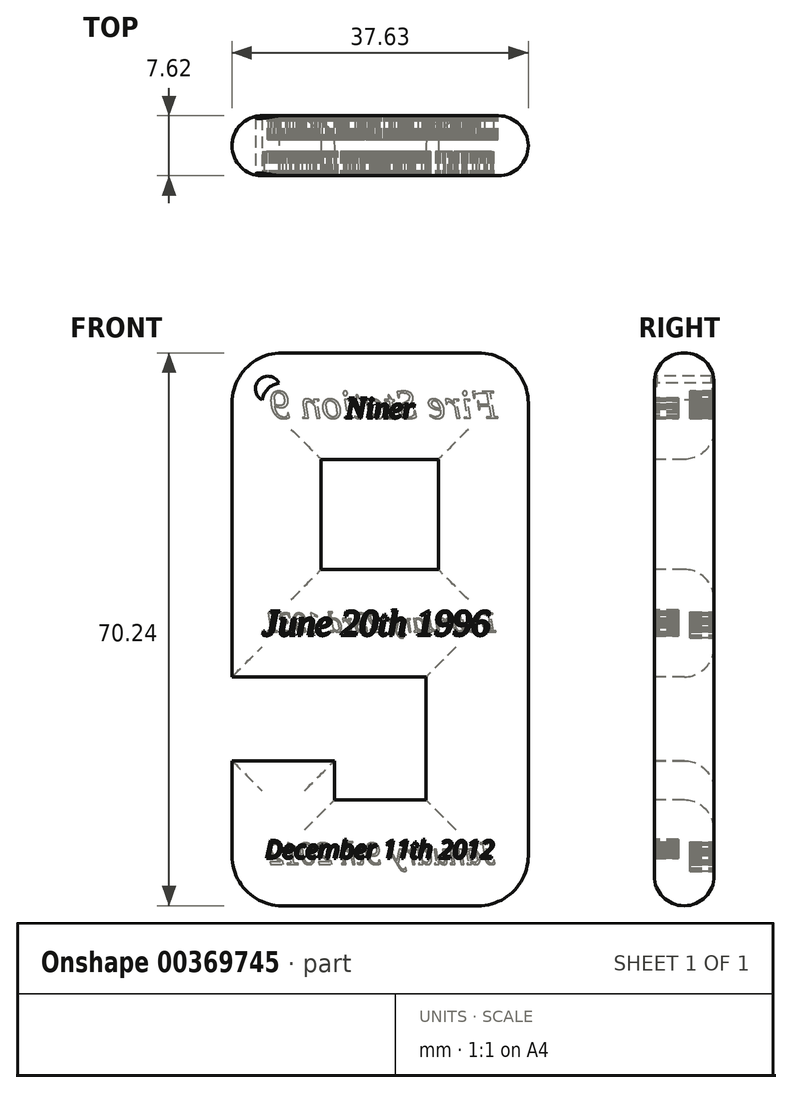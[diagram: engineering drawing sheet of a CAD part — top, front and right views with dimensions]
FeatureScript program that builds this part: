
annotation { "Feature Type Name" : "Feature", "Feature Type Description" : "" }
export const myFeature = defineFeature(function(context is Context, id is Id, definition is map)
    precondition{}
    {
        {
            var Q0;
            Q0=qCreatedBy(makeId("Front.planeOp"),FACE);
            var sketch = newSketch(context, id + "F0", { "sketchPlane" : qUnion([Q0])});
            skLineSegment(sketch, "E0.bottom", {"start": v(-12.42, 34.84) * mm, "end": v(12.5, 34.84) * mm});
            skLineSegment(sketch, "E0.top", {"start": v(-12.42, -35.4) * mm, "end": v(12.5, -35.4) * mm});
            skLineSegment(sketch, "E0.left", {"start": v(-18.77, 28.49) * mm, "end": v(-18.77, -29.05) * mm});
            skLineSegment(sketch, "E0.right", {"start": v(18.86, 28.49) * mm, "end": v(18.86, -29.05) * mm});
            skPoint(sketch, "E1.visualSharp", {"position": v(18.86, 34.84) * mm});
            skArc(sketch, "E1.filletArc", {"start": v(18.86, 28.49) * mm, "mid": v(17, 32.98) * mm, "end": v(12.5, 34.84) * mm});
            skPoint(sketch, "E2.visualSharp", {"position": v(18.86, -35.4) * mm});
            skArc(sketch, "E2.filletArc", {"start": v(12.5, -35.4) * mm, "mid": v(17, -33.54) * mm, "end": v(18.86, -29.05) * mm});
            skPoint(sketch, "E3.visualSharp", {"position": v(-18.77, -35.4) * mm});
            skArc(sketch, "E3.filletArc", {"start": v(-18.77, -29.05) * mm, "mid": v(-16.9, -33.54) * mm, "end": v(-12.42, -35.4) * mm});
            skPoint(sketch, "E4.visualSharp", {"position": v(-18.77, 34.84) * mm});
            skArc(sketch, "E4.filletArc", {"start": v(-12.42, 34.84) * mm, "mid": v(-16.9, 32.98) * mm, "end": v(-18.77, 28.49) * mm});
            skSolve(sketch);
        }
        {
            var Q0;
            Q0 = qSketchRegion(id + "F0", true);
            extrude(context, id + "F1", {"entities" : qUnion([Q0]), "depth" : 7.62 * mm});
        }
        {
            var Q0;
            Q0=makeQuery(id+"F1.opExtrude","CAP_FACE",FACE,{"disambiguationData":[OSD([sQuery(id+"F0.wireOp",EDGE,"E0.bottom"),sQuery(id+"F0.wireOp",EDGE,"E0.top"),sQuery(id+"F0.wireOp",EDGE,"E0.left"),sQuery(id+"F0.wireOp",EDGE,"E0.right")])],"isStart":false});
            var sketch = newSketch(context, id + "F2", { "sketchPlane" : qUnion([Q0])});
            skLineSegment(sketch, "E5.bottom", {"start": v(-7.43, 7.32) * mm, "end": v(7.43, 7.32) * mm});
            skLineSegment(sketch, "E5.top", {"start": v(-7.43, 21.3) * mm, "end": v(7.43, 21.3) * mm});
            skLineSegment(sketch, "E5.left", {"start": v(-7.43, 7.32) * mm, "end": v(-7.43, 21.3) * mm});
            skLineSegment(sketch, "E5.right", {"start": v(7.43, 7.32) * mm, "end": v(7.43, 21.3) * mm});
            skPoint(sketch, "E5.middle", {"position": v(0, 14.32) * mm});
            skSolve(sketch);
        }
        {
            var Q0;
            Q0 = qSketchRegion(id + "F2", true);
            extrude(context, id + "F3", {"entities" : qUnion([Q0]), "operationType" : NewBodyOperationType.REMOVE, "oppositeDirection" : true, "depth" : 7.62 * mm});
        }
        {
            var Q0;
            Q0=makeQuery(id+"F1.opExtrude","CAP_FACE",FACE,{"disambiguationData":[OSD([sQuery(id+"F0.wireOp",EDGE,"E0.bottom"),sQuery(id+"F0.wireOp",EDGE,"E0.top"),sQuery(id+"F0.wireOp",EDGE,"E0.left"),sQuery(id+"F0.wireOp",EDGE,"E0.right")])],"isStart":false});
            var sketch = newSketch(context, id + "F4", { "sketchPlane" : qUnion([Q0])});
            skLineSegment(sketch, "E6.bottom", {"start": v(-53.69, -16.98) * mm, "end": v(-3.13, -16.98) * mm});
            skLineSegment(sketch, "E6.top", {"start": v(-53.69, -6.33) * mm, "end": v(-3.13, -6.33) * mm});
            skLineSegment(sketch, "E6.left", {"start": v(-53.69, -16.98) * mm, "end": v(-53.69, -6.33) * mm});
            skLineSegment(sketch, "E6.right", {"start": v(-3.13, -16.98) * mm, "end": v(-3.13, -6.33) * mm});
            skPoint(sketch, "E6.middle", {"position": v(-28.4, -11.65) * mm});
            skLineSegment(sketch, "E7.bottom", {"start": v(5.88, -6.33) * mm, "end": v(-5.77, -6.33) * mm});
            skLineSegment(sketch, "E7.top", {"start": v(5.88, -21.97) * mm, "end": v(-5.77, -21.97) * mm});
            skLineSegment(sketch, "E7.left", {"start": v(5.88, -6.33) * mm, "end": v(5.88, -21.97) * mm});
            skLineSegment(sketch, "E7.right", {"start": v(-5.77, -6.33) * mm, "end": v(-5.77, -21.97) * mm});
            skSolve(sketch);
        }
        {
            var Q0;
            Q0 = qSketchRegion(id + "F4", true);
            extrude(context, id + "F5", {"entities" : qUnion([Q0]), "operationType" : NewBodyOperationType.REMOVE, "oppositeDirection" : true, "depth" : 7.62 * mm});
        }
        {
            var Q0;
            Q0=makeQuery(id+"F1.opExtrude","CAP_FACE",FACE,{"disambiguationData":[OSD([sQuery(id+"F0.wireOp",EDGE,"E0.bottom"),sQuery(id+"F0.wireOp",EDGE,"E0.top"),sQuery(id+"F0.wireOp",EDGE,"E0.left"),sQuery(id+"F0.wireOp",EDGE,"E0.right"),sQuery(id+"F0.wireOp",EDGE,"E1.filletArc"),sQuery(id+"F0.wireOp",EDGE,"E2.filletArc"),sQuery(id+"F0.wireOp",EDGE,"E3.filletArc"),sQuery(id+"F0.wireOp",EDGE,"E4.filletArc")])],"isStart":false});
            var sketch = newSketch(context, id + "F6", { "sketchPlane" : qUnion([Q0])});
            skPoint(sketch, "E8", {"position": v(0, 34.84) * mm});
            skPoint(sketch, "E9", {"position": v(0, 21.3) * mm});
            skPoint(sketch, "E10", {"position": v(-7.43, 14.32) * mm});
            skPoint(sketch, "E11", {"position": v(-18.77, 14.32) * mm});
            skPoint(sketch, "E12", {"position": v(7.43, 14.32) * mm});
            skPoint(sketch, "E13", {"position": v(18.86, 14.32) * mm});
            skPoint(sketch, "E14", {"position": v(0, -6.33) * mm});
            skPoint(sketch, "E15", {"position": v(0, 7.32) * mm});
            skSolve(sketch);
        }
        {
            var Q0;
            {var subQ0=sQuery(id+"F0.wireOp",EDGE,"E4.filletArc");var subQ1=sQuery(id+"F0.wireOp",EDGE,"E0.left");Q0=makeQuery(id+"F5.boolean.opBoolean","SPLIT",EDGE,{"disambiguationData":[TD([makeQuery(id+"F1.opExtrude","SWEPT_FACE",FACE,{"disambiguationData":[OSD([subQ0])]})])],"derivedFrom":makeQuery(id+"F1.opExtrude","CAP_EDGE",EDGE,{"disambiguationData":[OSD([subQ1])],"isStart":false})});}
            var Q1;
            Q1=makeQuery(id+"F5.boolean.opBoolean","COPY",EDGE,{"derivedFrom":makeQuery(id+"F5.opExtrude","CAP_EDGE",EDGE,{"disambiguationData":[OSD([sQuery(id+"F4.wireOp",EDGE,"E6.top"),sQuery(id+"F4.wireOp",EDGE,"E7.bottom")])],"isStart":true})});
            var Q2;
            {var subQ0=sQuery(id+"F0.wireOp",EDGE,"E3.filletArc");var subQ1=sQuery(id+"F0.wireOp",EDGE,"E0.left");Q2=makeQuery(id+"F5.boolean.opBoolean","SPLIT",EDGE,{"disambiguationData":[TD([makeQuery(id+"F1.opExtrude","SWEPT_FACE",FACE,{"disambiguationData":[OSD([subQ0])]})])],"derivedFrom":makeQuery(id+"F1.opExtrude","CAP_EDGE",EDGE,{"disambiguationData":[OSD([subQ1])],"isStart":false})});}
            var Q3;
            Q3=makeQuery(id+"F5.boolean.opBoolean","COPY",EDGE,{"derivedFrom":makeQuery(id+"F5.opExtrude","CAP_EDGE",EDGE,{"disambiguationData":[OSD([sQuery(id+"F4.wireOp",EDGE,"E6.bottom")])],"isStart":true})});
            var Q4;
            Q4=makeQuery(id+"F5.boolean.opBoolean","COPY",EDGE,{"derivedFrom":makeQuery(id+"F5.opExtrude","CAP_EDGE",EDGE,{"disambiguationData":[OSD([sQuery(id+"F4.wireOp",EDGE,"E7.right")])],"isStart":true})});
            var Q5;
            Q5=makeQuery(id+"F5.boolean.opBoolean","COPY",EDGE,{"derivedFrom":makeQuery(id+"F5.opExtrude","CAP_EDGE",EDGE,{"disambiguationData":[OSD([sQuery(id+"F4.wireOp",EDGE,"E7.top")])],"isStart":true})});
            var Q6;
            Q6=makeQuery(id+"F5.boolean.opBoolean","COPY",EDGE,{"derivedFrom":makeQuery(id+"F5.opExtrude","CAP_EDGE",EDGE,{"disambiguationData":[OSD([sQuery(id+"F4.wireOp",EDGE,"E7.left")])],"isStart":true})});
            var Q7;
            Q7=makeQuery(id+"F3.boolean.opBoolean","COPY",EDGE,{"derivedFrom":makeQuery(id+"F3.opExtrude","CAP_EDGE",EDGE,{"disambiguationData":[OSD([sQuery(id+"F2.wireOp",EDGE,"E5.left")])],"isStart":true})});
            var Q8;
            Q8=makeQuery(id+"F3.boolean.opBoolean","COPY",EDGE,{"derivedFrom":makeQuery(id+"F3.opExtrude","CAP_EDGE",EDGE,{"disambiguationData":[OSD([sQuery(id+"F2.wireOp",EDGE,"E5.top")])],"isStart":true})});
            var Q9;
            Q9=makeQuery(id+"F3.boolean.opBoolean","COPY",EDGE,{"derivedFrom":makeQuery(id+"F3.opExtrude","CAP_EDGE",EDGE,{"disambiguationData":[OSD([sQuery(id+"F2.wireOp",EDGE,"E5.right")])],"isStart":true})});
            var Q10;
            Q10=makeQuery(id+"F3.boolean.opBoolean","COPY",EDGE,{"derivedFrom":makeQuery(id+"F3.opExtrude","CAP_EDGE",EDGE,{"disambiguationData":[OSD([sQuery(id+"F2.wireOp",EDGE,"E5.bottom")])],"isStart":true})});
            fillet(context, id + "F7", {"entities" : qUnion([Q0, Q1, Q2, Q3, Q4, Q5, Q6, Q7, Q8, Q9, Q10]), "radius" : 3.8 * mm, "tangentPropagation" : true, "allowEdgeOverflow" : false});
        }
        {
            var Q0;
            Q0=makeQuery(id+"F1.opExtrude","CAP_FACE",FACE,{"disambiguationData":[OSD([sQuery(id+"F0.wireOp",EDGE,"E0.bottom"),sQuery(id+"F0.wireOp",EDGE,"E0.top"),sQuery(id+"F0.wireOp",EDGE,"E0.left"),sQuery(id+"F0.wireOp",EDGE,"E0.right"),sQuery(id+"F0.wireOp",EDGE,"E1.filletArc"),sQuery(id+"F0.wireOp",EDGE,"E2.filletArc"),sQuery(id+"F0.wireOp",EDGE,"E3.filletArc"),sQuery(id+"F0.wireOp",EDGE,"E4.filletArc")])],"isStart":true});
            fillet(context, id + "F8", {"entities" : qUnion([Q0]), "radius" : 3.8 * mm, "tangentPropagation" : true, "allowEdgeOverflow" : false});
        }
        {
            var Q0;
            Q0=makeQuery(id+"F1.opExtrude","CAP_FACE",FACE,{"disambiguationData":[OSD([sQuery(id+"F0.wireOp",EDGE,"E0.bottom"),sQuery(id+"F0.wireOp",EDGE,"E0.top"),sQuery(id+"F0.wireOp",EDGE,"E0.left"),sQuery(id+"F0.wireOp",EDGE,"E0.right"),sQuery(id+"F0.wireOp",EDGE,"E1.filletArc"),sQuery(id+"F0.wireOp",EDGE,"E2.filletArc"),sQuery(id+"F0.wireOp",EDGE,"E3.filletArc"),sQuery(id+"F0.wireOp",EDGE,"E4.filletArc")])],"isStart":true});
            var sketch = newSketch(context, id + "F9", { "sketchPlane" : qUnion([Q0])});
            skText(sketch, "E16", { "text": "Fire Station 9", "fontName": "Tinos-Italic.ttf"});
            const initialGuessF9  = {"E16": [-0.015, 0.02653, 1, 0, 0.00375]};
            skSetInitialGuess(sketch, initialGuessF9);
            skSolve(sketch);
        }
        {
            var Q0;
            Q0 = qSketchRegion(id + "F9", true);
            extrude(context, id + "F10", {"entities" : qUnion([Q0]), "operationType" : NewBodyOperationType.REMOVE, "oppositeDirection" : true, "depth" : 3.05 * mm});
        }
        {
            var Q0;
            {var subQ0=sQuery(id+"F0.wireOp",EDGE,"E4.filletArc");var subQ1=sQuery(id+"F0.wireOp",EDGE,"E3.filletArc");var subQ2=sQuery(id+"F0.wireOp",EDGE,"E2.filletArc");var subQ3=sQuery(id+"F0.wireOp",EDGE,"E1.filletArc");var subQ4=sQuery(id+"F0.wireOp",EDGE,"E0.right");var subQ5=sQuery(id+"F0.wireOp",EDGE,"E0.left");var subQ6=sQuery(id+"F0.wireOp",EDGE,"E0.top");var subQ7=sQuery(id+"F0.wireOp",EDGE,"E0.bottom");var subQ8=makeQuery(id+"F1.opExtrude","CAP_FACE",FACE,{"disambiguationData":[OSD([subQ7,subQ6,subQ5,subQ4,subQ3,subQ2,subQ1,subQ0])],"isStart":false});Q0=makeQuery(id+"FmLQ3wYA3wTMYqe_1.boolean.opBoolean","SPLIT",FACE,{"disambiguationData":[TD([makeQuery(id+"F7.opFillet","BLEND_FACE",FACE,{"disambiguationData":[OSD([subQ7])]})])],"derivedFrom":subQ8});}
            var sketch = newSketch(context, id + "F11", { "sketchPlane" : qUnion([Q0])});
            skCircle(sketch, "E17", {"center": v(-14.21, 30.28) * mm, "radius": 1.6 * mm});
            skSolve(sketch);
        }
        {
            var Q0;
            {var subQ0=sQuery(id+"F11.wireOp",EDGE,"E17");var subQ1=sQuery(id+"F0.wireOp",EDGE,"E4.filletArc");var subQ2=makeQuery(id+"F7.opFillet","BLEND_EDGE",EDGE,{"blendedFrom":[makeQuery(id+"F1.opExtrude","CAP_EDGE",EDGE,{"disambiguationData":[OSD([subQ1])],"isStart":false}),makeQuery(id+"F1.opExtrude","CAP_FACE",FACE,{"disambiguationData":[OSD([sQuery(id+"F0.wireOp",EDGE,"E0.bottom"),sQuery(id+"F0.wireOp",EDGE,"E0.top"),sQuery(id+"F0.wireOp",EDGE,"E0.left"),sQuery(id+"F0.wireOp",EDGE,"E0.right"),sQuery(id+"F0.wireOp",EDGE,"E1.filletArc"),sQuery(id+"F0.wireOp",EDGE,"E2.filletArc"),sQuery(id+"F0.wireOp",EDGE,"E3.filletArc"),subQ1])],"isStart":false})],"blendedInto":[makeQuery(id+"F1.opExtrude","CAP_FACE",FACE,{"disambiguationData":[OSD([sQuery(id+"F0.wireOp",EDGE,"E0.bottom"),sQuery(id+"F0.wireOp",EDGE,"E0.top"),sQuery(id+"F0.wireOp",EDGE,"E0.left"),sQuery(id+"F0.wireOp",EDGE,"E0.right"),sQuery(id+"F0.wireOp",EDGE,"E1.filletArc"),sQuery(id+"F0.wireOp",EDGE,"E2.filletArc"),sQuery(id+"F0.wireOp",EDGE,"E3.filletArc"),subQ1])],"isStart":false})]});var subQ3=makeQuery(id+"F11.imprint","INTERSECT",VERTEX,{"disambiguationData":[OD(0.0)],"derivedFrom":[subQ2,subQ0]});Q0=makeQuery(id+"F11.imprint","IMPRINT",FACE,{"disambiguationData":[TD([[makeQuery(id+"F11.imprint","IMPRINT",EDGE,{"disambiguationData":[TD([[subQ3,-1.0]])],"derivedFrom":subQ0}),1.0]])]});}
            extrude(context, id + "F12", {"entities" : qUnion([Q0]), "operationType" : NewBodyOperationType.REMOVE, "oppositeDirection" : true, "depth" : 25.4 * mm});
        }
        {
            var Q0;
            Q0=makeQuery(id+"F1.opExtrude","CAP_FACE",FACE,{"disambiguationData":[OSD([sQuery(id+"F0.wireOp",EDGE,"E0.bottom"),sQuery(id+"F0.wireOp",EDGE,"E0.top"),sQuery(id+"F0.wireOp",EDGE,"E0.left"),sQuery(id+"F0.wireOp",EDGE,"E0.right"),sQuery(id+"F0.wireOp",EDGE,"E1.filletArc"),sQuery(id+"F0.wireOp",EDGE,"E2.filletArc"),sQuery(id+"F0.wireOp",EDGE,"E3.filletArc"),sQuery(id+"F0.wireOp",EDGE,"E4.filletArc")])],"isStart":false});
            var sketch = newSketch(context, id + "F13", { "sketchPlane" : qUnion([Q0])});
            skText(sketch, "E18", { "text": "Niner", "fontName": "Tinos-Italic.ttf"});
            const initialGuessF13  = {"E18": [-0.00433, 0.02656, 1, 0, 0.00276]};
            skSetInitialGuess(sketch, initialGuessF13);
            skSolve(sketch);
        }
        {
            var Q0;
            Q0=makeQuery(id+"F13.imprint","IMPRINT",FACE,{"disambiguationData":[TD([[makeQuery(id+"F13.imprint","IMPRINT",EDGE,{"derivedFrom":sQuery(id+"F13.wireOp",EDGE,"E18.sketch_text.stroke-0")}),1.0]])]});
            var sketch = newSketch(context, id + "F14", { "sketchPlane" : qUnion([Q0])});
            skText(sketch, "E19", { "text": "December 11th 2012", "fontName": "OpenSans-Italic.ttf"});
            const initialGuessF14  = {"E19": [-0.01452, -0.02938, 1, 0, 0.00228]};
            skSetInitialGuess(sketch, initialGuessF14);
            skSolve(sketch);
        }
        {
            var Q0;
            Q0 = qSketchRegion(id + "F14", true);
            extrude(context, id + "F15", {"entities" : qUnion([Q0]), "operationType" : NewBodyOperationType.REMOVE, "oppositeDirection" : true, "depth" : 3.05 * mm});
        }
        {
            var Q0;
            Q0 = qSketchRegion(id + "F13", true);
            extrude(context, id + "F16", {"entities" : qUnion([Q0]), "operationType" : NewBodyOperationType.REMOVE, "oppositeDirection" : true, "depth" : 3.05 * mm});
        }
        {
            var Q0;
            {var subQ0=sQuery(id+"F0.wireOp",EDGE,"E3.filletArc");var subQ1=sQuery(id+"F0.wireOp",EDGE,"E2.filletArc");var subQ2=sQuery(id+"F0.wireOp",EDGE,"E4.filletArc");var subQ3=sQuery(id+"F0.wireOp",EDGE,"E0.bottom");var subQ4=sQuery(id+"F0.wireOp",EDGE,"E0.top");var subQ5=sQuery(id+"F0.wireOp",EDGE,"E1.filletArc");var subQ6=sQuery(id+"F0.wireOp",EDGE,"E0.right");var subQ9=sQuery(id+"F0.wireOp",EDGE,"E0.left");Q0=makeQuery(id+"F10.boolean.opBoolean","SPLIT",FACE,{"disambiguationData":[TD([makeQuery(id+"F7.opFillet","BLEND_FACE",FACE,{"disambiguationData":[OSD([subQ3])]})])],"derivedFrom":makeQuery(id+"F1.opExtrude","CAP_FACE",FACE,{"disambiguationData":[OSD([subQ3,subQ4,subQ9,subQ6,subQ5,subQ1,subQ0,subQ2])],"isStart":true})});}
            var sketch = newSketch(context, id + "F17", { "sketchPlane" : qUnion([Q0])});
            skText(sketch, "E20", { "text": "February 23rd 1931", "fontName": "Tinos-Italic.ttf"});
            const initialGuessF17  = {"E20": [-0.01473, -0.0006, 1, 0, 0.00259]};
            skSetInitialGuess(sketch, initialGuessF17);
            skSolve(sketch);
        }
        {
            var Q0;
            Q0=makeQuery(id+"F17.imprint","IMPRINT",FACE,{"disambiguationData":[TD([[makeQuery(id+"F17.imprint","IMPRINT",EDGE,{"derivedFrom":sQuery(id+"F17.wireOp",EDGE,"E20.sketch_text.stroke-0")}),1.0]])]});
            var sketch = newSketch(context, id + "F18", { "sketchPlane" : qUnion([Q0])});
            skText(sketch, "E21", { "text": "January 9th 2012", "fontName": "Tinos-Italic.ttf"});
            const initialGuessF18  = {"E21": [-0.0147, -0.03013, 1, 0, 0.00296]};
            skSetInitialGuess(sketch, initialGuessF18);
            skSolve(sketch);
        }
        {
            var Q0;
            Q0 = qSketchRegion(id + "F17", true);
            extrude(context, id + "F19", {"entities" : qUnion([Q0]), "operationType" : NewBodyOperationType.REMOVE, "oppositeDirection" : true, "depth" : 3.05 * mm});
        }
        {
            var Q0;
            Q0 = qSketchRegion(id + "F18", true);
            extrude(context, id + "F20", {"entities" : qUnion([Q0]), "operationType" : NewBodyOperationType.REMOVE, "oppositeDirection" : true, "depth" : 3.05 * mm});
        }
        {
            var Q0;
            {var subQ151=sQuery(id+"F0.wireOp",EDGE,"E0.bottom");var subQ152=makeQuery(id+"F7.opFillet","BLEND_FACE",FACE,{"disambiguationData":[OSD([subQ151])]});var subQ155=sQuery(id+"F0.wireOp",EDGE,"E0.top");var subQ159=sQuery(id+"F0.wireOp",EDGE,"E0.right");var subQ163=sQuery(id+"F0.wireOp",EDGE,"E1.filletArc");var subQ167=sQuery(id+"F0.wireOp",EDGE,"E2.filletArc");var subQ171=sQuery(id+"F0.wireOp",EDGE,"E3.filletArc");var subQ194=sQuery(id+"F0.wireOp",EDGE,"E4.filletArc");var subQ195=sQuery(id+"F0.wireOp",EDGE,"E0.left");var subQ196=makeQuery(id+"F1.opExtrude","CAP_FACE",FACE,{"disambiguationData":[OSD([subQ151,subQ155,subQ195,subQ159,subQ163,subQ167,subQ171,subQ194])],"isStart":false});Q0=makeQuery(id+"F16.boolean.opBoolean","SPLIT",FACE,{"disambiguationData":[TD([subQ152])],"derivedFrom":makeQuery(id+"F15.boolean.opBoolean","SPLIT",FACE,{"disambiguationData":[TD([subQ152])],"derivedFrom":subQ196})});}
            var sketch = newSketch(context, id + "F21", { "sketchPlane" : qUnion([Q0])});
            skText(sketch, "E22", { "text": "June 20th 1996", "fontName": "Tinos-Italic.ttf"});
            const initialGuessF21  = {"E22": [-0.01496, -0.00105, 1, 0, 0.00338]};
            skSetInitialGuess(sketch, initialGuessF21);
            skSolve(sketch);
        }
        {
            var Q0;
            Q0 = qSketchRegion(id + "F21", true);
            extrude(context, id + "F22", {"entities" : qUnion([Q0]), "operationType" : NewBodyOperationType.REMOVE, "oppositeDirection" : true, "depth" : 3.05 * mm});
        }
    });
